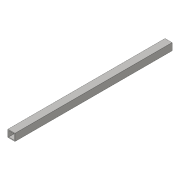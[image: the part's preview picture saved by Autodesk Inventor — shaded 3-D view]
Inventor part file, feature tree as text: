
AUTODESK INVENTOR PART (.ipt)
format: ipt  version: 2016 (Build 200138000, 138)  size: 73,728 bytes
history: native  units: in
note: dims shown in document units (in); Inventor stores cm internally (conversion verified against a paired STEP export)
features: extrude x1, shell x1, sketch x1
ambient origin geometry x8: Origin, YZ Plane, XZ Plane, XY Plane, X Axis, Y Axis, Z Axis, Center Point
bodies: Solid1 (feature_tree)
feature tree (3):
  extrude  "Extrusion1"  Depth=1.0in
  shell  "Shell1"  Thickness=22.0in
  sketch  "Sketch1"  dims[d0=1.0in d1=1.0in d2=22.0in d3=0.0in d4=0.1in]
